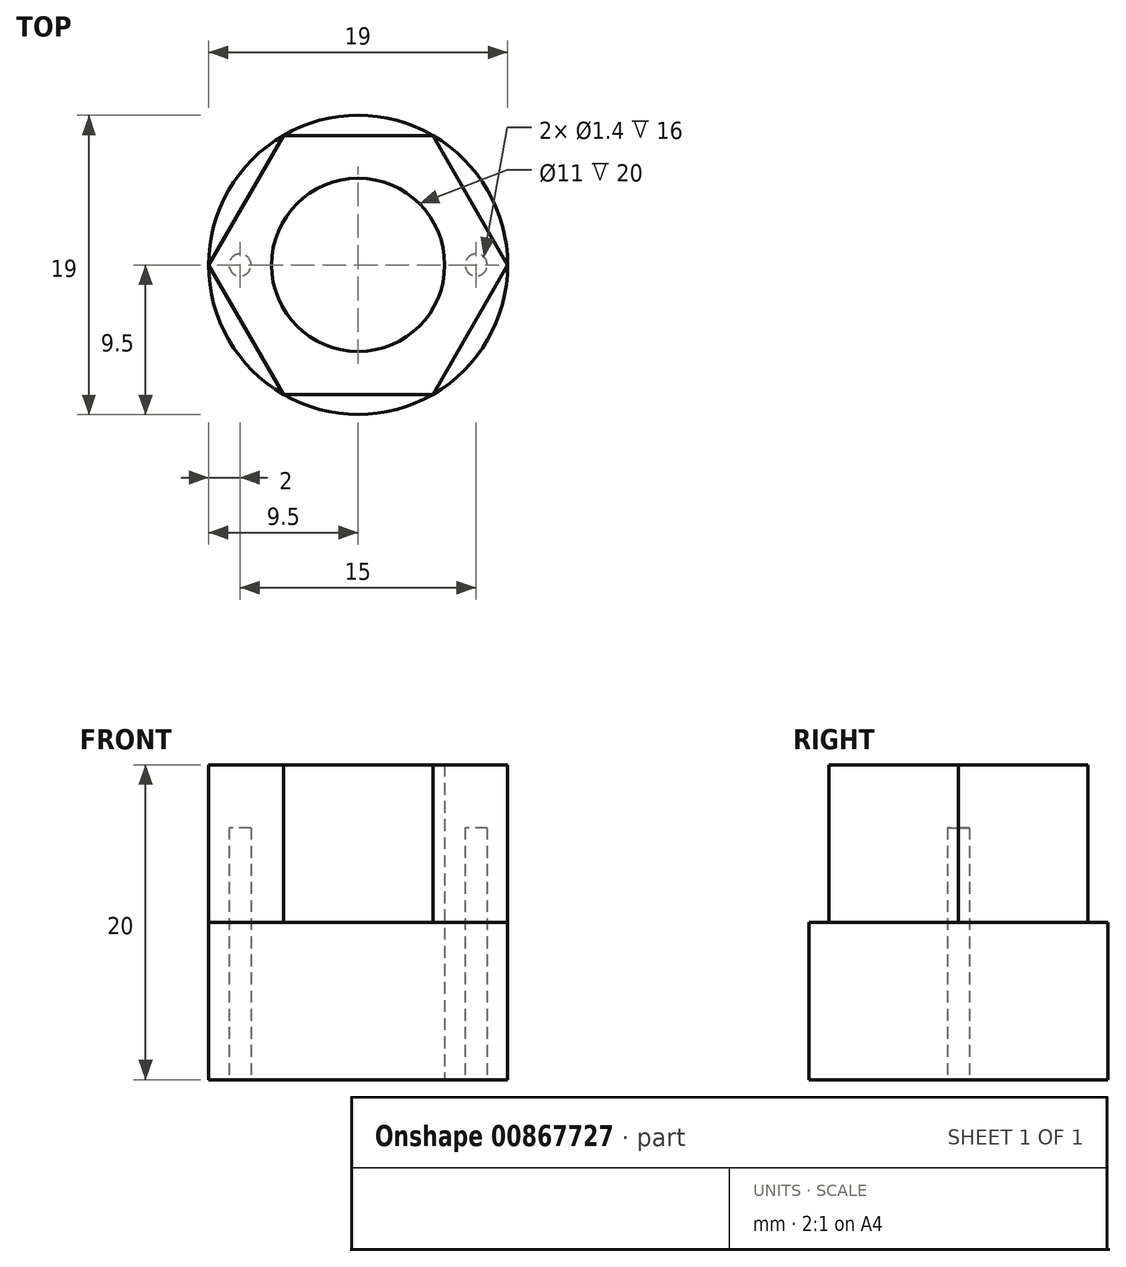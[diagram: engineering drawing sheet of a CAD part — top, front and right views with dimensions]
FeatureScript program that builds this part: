
annotation { "Feature Type Name" : "Feature", "Feature Type Description" : "" }
export const myFeature = defineFeature(function(context is Context, id is Id, definition is map)
    precondition{}
    {
        {
            var Q0;
            Q0=qCreatedBy(makeId("Top.planeOp"),FACE);
            var sketch = newSketch(context, id + "F0", { "sketchPlane" : qUnion([Q0])});
            skCircle(sketch, "E0", {"center": v(0, 0) * mm, "radius": 7.5 * mm, "construction": true});
            skCircle(sketch, "E1", {"center": v(7.5, 0) * mm, "radius": 0.7 * mm});
            skCircle(sketch, "E2", {"center": v(-7.5, 0) * mm, "radius": 0.7 * mm});
            skCircle(sketch, "E3", {"center": v(0, 0) * mm, "radius": 9.5 * mm});
            skCircle(sketch, "E4", {"center": v(0, 0) * mm, "radius": 5.5 * mm});
            skSolve(sketch);
        }
        {
            var Q0;
            Q0=makeQuery(id+"F0.imprint","IMPRINT",FACE,{"disambiguationData":[TD([[makeQuery(id+"F0.imprint","IMPRINT",EDGE,{"derivedFrom":sQuery(id+"F0.wireOp",EDGE,"E1")}),-1.0]])]});
            extrude(context, id + "F1", {"entities" : qUnion([Q0]), "depth" : 10 * mm, "offsetDistance" : 25 * mm});
        }
        {
            var Q0;
            Q0=makeQuery(id+"F0.imprint","IMPRINT",FACE,{"disambiguationData":[TD([[makeQuery(id+"F0.imprint","IMPRINT",EDGE,{"derivedFrom":sQuery(id+"F0.wireOp",EDGE,"E4")}),1.0]])]});
            extrude(context, id + "F2", {"entities" : qUnion([Q0]), "operationType" : NewBodyOperationType.REMOVE, "depth" : 5 * mm, "offsetDistance" : 25 * mm});
        }
        {
            var Q0;
            Q0=makeQuery(id+"F1.opExtrude","CAP_FACE",FACE,{"disambiguationData":[OSD([sQuery(id+"F0.wireOp",EDGE,"E1"),sQuery(id+"F0.wireOp",EDGE,"E2"),sQuery(id+"F0.wireOp",EDGE,"E3")])],"isStart":false});
            var sketch = newSketch(context, id + "F3", { "sketchPlane" : qUnion([Q0])});
            skPoint(sketch, "E5.0", {"position": v(0, 0) * mm});
            skCircle(sketch, "E6.0", {"center": v(0, 0) * mm, "radius": 9.5 * mm, "construction": true});
            skLineSegment(sketch, "E7.0", {"start": v(9.5, 0) * mm, "end": v(4.75, -8.23) * mm});
            skLineSegment(sketch, "E7.1", {"start": v(4.75, -8.23) * mm, "end": v(-4.75, -8.23) * mm});
            skLineSegment(sketch, "E7.2", {"start": v(-4.75, -8.23) * mm, "end": v(-9.5, 0) * mm});
            skLineSegment(sketch, "E7.3", {"start": v(-9.5, 0) * mm, "end": v(-4.75, 8.23) * mm});
            skLineSegment(sketch, "E7.4", {"start": v(-4.75, 8.23) * mm, "end": v(4.75, 8.23) * mm});
            skLineSegment(sketch, "E7.5", {"start": v(4.75, 8.23) * mm, "end": v(9.5, 0) * mm});
            skSolve(sketch);
        }
        {
            var Q0;
            Q0=makeQuery(id+"F3.imprint","IMPRINT",FACE,{"disambiguationData":[TD([[makeQuery(id+"F3.imprint","IMPRINT",EDGE,{"derivedFrom":sQuery(id+"F3.wireOp",EDGE,"E7.0")}),-1.0]])]});
            extrude(context, id + "F4", {"entities" : qUnion([Q0]), "operationType" : NewBodyOperationType.ADD, "depth" : 6 * mm, "offsetDistance" : 25 * mm});
        }
        {
            var Q0;
            Q0=makeQuery(id+"F4.opExtrude","CAP_FACE",FACE,{"disambiguationData":[OSD([sQuery(id+"F0.wireOp",EDGE,"E1"),sQuery(id+"F0.wireOp",EDGE,"E2"),sQuery(id+"F3.wireOp",EDGE,"E7.0"),sQuery(id+"F3.wireOp",EDGE,"E7.1"),sQuery(id+"F3.wireOp",EDGE,"E7.2"),sQuery(id+"F3.wireOp",EDGE,"E7.3"),sQuery(id+"F3.wireOp",EDGE,"E7.4"),sQuery(id+"F3.wireOp",EDGE,"E7.5")])],"isStart":false});
            var sketch = newSketch(context, id + "F5", { "sketchPlane" : qUnion([Q0])});
            skLineSegment(sketch, "E8.0.0", {"start": v(9.5, 0) * mm, "end": v(4.75, 8.23) * mm});
            skLineSegment(sketch, "E8.0.1", {"start": v(4.75, 8.23) * mm, "end": v(-4.75, 8.23) * mm});
            skLineSegment(sketch, "E8.0.2", {"start": v(-4.75, 8.23) * mm, "end": v(-9.5, 0) * mm});
            skLineSegment(sketch, "E8.0.3", {"start": v(-9.5, 0) * mm, "end": v(-4.75, -8.23) * mm});
            skLineSegment(sketch, "E8.0.4", {"start": v(-4.75, -8.23) * mm, "end": v(4.75, -8.23) * mm});
            skLineSegment(sketch, "E8.0.5", {"start": v(4.75, -8.23) * mm, "end": v(9.5, 0) * mm});
            skSolve(sketch);
        }
        {
            var Q0;
            Q0=makeQuery(id+"F5.imprint","IMPRINT",FACE,{"disambiguationData":[TD([[makeQuery(id+"F5.imprint","IMPRINT",EDGE,{"derivedFrom":makeQuery(id+"F4.opExtrude","CAP_EDGE",EDGE,{"disambiguationData":[OSD([sQuery(id+"F0.wireOp",EDGE,"E2")])],"isStart":false})}),1.0]])]});
            var Q1;
            Q1=makeQuery(id+"F5.imprint","IMPRINT",FACE,{"disambiguationData":[TD([[makeQuery(id+"F5.imprint","IMPRINT",EDGE,{"derivedFrom":makeQuery(id+"F4.opExtrude","CAP_EDGE",EDGE,{"disambiguationData":[OSD([sQuery(id+"F0.wireOp",EDGE,"E1")])],"isStart":false})}),1.0]])]});
            var Q2;
            Q2=makeQuery(id+"F5.imprint","IMPRINT",FACE,{"disambiguationData":[TD([[makeQuery(id+"F5.imprint","IMPRINT",EDGE,{"derivedFrom":sQuery(id+"F5.wireOp",EDGE,"E8.0.0")}),-1.0]])]});
            extrude(context, id + "F6", {"entities" : qUnion([Q0, Q1, Q2]), "operationType" : NewBodyOperationType.ADD, "depth" : 4 * mm, "offsetDistance" : 25 * mm});
        }
    });
